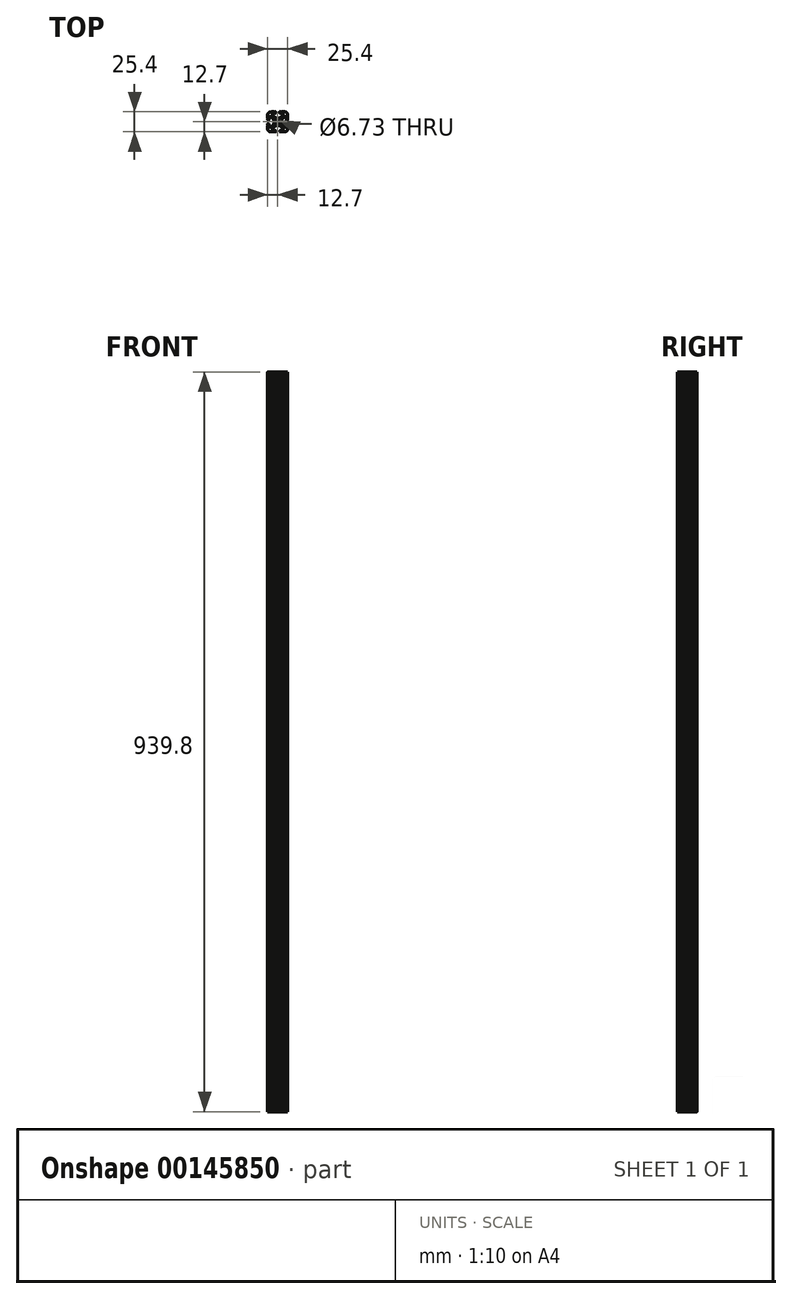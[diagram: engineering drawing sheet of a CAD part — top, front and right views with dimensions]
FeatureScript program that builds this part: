
annotation { "Feature Type Name" : "Feature", "Feature Type Description" : "" }
export const myFeature = defineFeature(function(context is Context, id is Id, definition is map)
    precondition{}
    {
        {
            var Q0;
            Q0=qCreatedBy(makeId("Top.planeOp"),FACE);
            var sketch = newSketch(context, id + "F0", { "sketchPlane" : qUnion([Q0])});
            skCircle(sketch, "E0", {"center": v(-12.7, 12.7) * mm, "radius": 3.36 * mm});
            skLineSegment(sketch, "E1.bottom", {"start": v(-11.24, 17.64) * mm, "end": v(-14.16, 17.64) * mm});
            skLineSegment(sketch, "E1.top", {"start": v(-11.24, 7.76) * mm, "end": v(-14.16, 7.76) * mm});
            skLineSegment(sketch, "E1.left", {"start": v(-7.76, 14.16) * mm, "end": v(-7.76, 11.24) * mm});
            skLineSegment(sketch, "E1.right", {"start": v(-17.64, 14.16) * mm, "end": v(-17.64, 11.24) * mm});
            skPoint(sketch, "E2.visualSharp", {"position": v(-25.4, 25.4) * mm});
            skPoint(sketch, "E3.visualSharp", {"position": v(0, 25.4) * mm});
            skPoint(sketch, "E4.visualSharp", {"position": v(0, 0) * mm});
            skPoint(sketch, "E5.visualSharp", {"position": v(-25.4, 0) * mm});
            skLineSegment(sketch, "E6.0", {"start": v(-18.7, 20.6) * mm, "end": v(-16.85, 18.76) * mm});
            skLineSegment(sketch, "E7.0", {"start": v(-20.6, 18.7) * mm, "end": v(-18.76, 16.85) * mm});
            skPoint(sketch, "E8.orphan", {"position": v(-23.85, 1.55) * mm});
            skPoint(sketch, "E9.orphan", {"position": v(-23.85, 23.85) * mm});
            skPoint(sketch, "E10.orphan", {"position": v(-1.55, 23.85) * mm});
            skPoint(sketch, "E11.orphan", {"position": v(-1.55, 1.55) * mm});
            skLineSegment(sketch, "E12", {"start": v(-8.55, 6.64) * mm, "end": v(-6.7, 4.8) * mm});
            skLineSegment(sketch, "E13.0", {"start": v(-18.7, 4.8) * mm, "end": v(-16.85, 6.64) * mm});
            skLineSegment(sketch, "E14.0", {"start": v(-20.6, 6.7) * mm, "end": v(-18.76, 8.55) * mm});
            skLineSegment(sketch, "E15.0", {"start": v(-8.55, 18.76) * mm, "end": v(-6.7, 20.6) * mm});
            skPoint(sketch, "E16.visualSharp", {"position": v(-23.85, 21.95) * mm});
            skArc(sketch, "E16.filletArc", {"start": v(-20.6, 18.7) * mm, "mid": v(-22.68, 19.1) * mm, "end": v(-23.85, 17.35) * mm});
            skPoint(sketch, "E17.visualSharp", {"position": v(-21.95, 23.85) * mm});
            skArc(sketch, "E17.filletArc", {"start": v(-17.35, 23.85) * mm, "mid": v(-19.1, 22.68) * mm, "end": v(-18.7, 20.6) * mm});
            skPoint(sketch, "E18.visualSharp", {"position": v(-5.34, 23.85) * mm});
            skLineSegment(sketch, "E19", {"start": v(-17.35, 23.85) * mm, "end": v(-15.58, 23.85) * mm});
            skLineSegment(sketch, "E20", {"start": v(-23.85, 17.35) * mm, "end": v(-23.85, 15.62) * mm});
            skLineSegment(sketch, "E21", {"start": v(-8.05, 1.55) * mm, "end": v(-9.78, 1.55) * mm});
            skArc(sketch, "E22.filletArc", {"start": v(-6.7, 20.6) * mm, "mid": v(-6.3, 22.68) * mm, "end": v(-8.05, 23.85) * mm});
            skPoint(sketch, "E23.visualSharp", {"position": v(-1.55, 3.45) * mm});
            skPoint(sketch, "E24.visualSharp", {"position": v(-3.45, 1.55) * mm});
            skArc(sketch, "E24.filletArc", {"start": v(-8.05, 1.55) * mm, "mid": v(-6.3, 2.73) * mm, "end": v(-6.7, 4.8) * mm});
            skArc(sketch, "E25.filletArc", {"start": v(-18.7, 4.8) * mm, "mid": v(-19.1, 2.73) * mm, "end": v(-17.35, 1.55) * mm});
            skArc(sketch, "E26.filletArc", {"start": v(-23.85, 8.05) * mm, "mid": v(-22.68, 6.3) * mm, "end": v(-20.6, 6.7) * mm});
            skLineSegment(sketch, "E27.bottom", {"start": v(-4.9, 0) * mm, "end": v(-8.05, 0) * mm});
            skLineSegment(sketch, "E27.top", {"start": v(-4.92, 25.4) * mm, "end": v(-8.05, 25.4) * mm});
            skLineSegment(sketch, "E27.left", {"start": v(0, 4.9) * mm, "end": v(0, 8.05) * mm});
            skLineSegment(sketch, "E27.right", {"start": v(-25.4, 4.9) * mm, "end": v(-25.4, 8.05) * mm});
            skArc(sketch, "E28.filletArc", {"start": v(-25.4, 3.81) * mm, "mid": v(-24.28, 1.12) * mm, "end": v(-21.59, 0) * mm});
            skArc(sketch, "E29.filletArc", {"start": v(-3.81, 0) * mm, "mid": v(-1.12, 1.12) * mm, "end": v(0, 3.8) * mm});
            skArc(sketch, "E30.filletArc", {"start": v(0, 21.59) * mm, "mid": v(-1.12, 24.28) * mm, "end": v(-3.8, 25.4) * mm});
            skArc(sketch, "E31.filletArc", {"start": v(-21.59, 25.4) * mm, "mid": v(-24.28, 24.28) * mm, "end": v(-25.4, 21.59) * mm});
            skPoint(sketch, "E32.newPointA", {"position": v(-17.64, 7.76) * mm});
            skArc(sketch, "E32.filletArc", {"start": v(-14.16, 7.76) * mm, "mid": v(-15.62, 7.47) * mm, "end": v(-16.85, 6.64) * mm});
            skPoint(sketch, "E33.newPointA", {"position": v(-7.76, 7.76) * mm});
            skArc(sketch, "E33.filletArc", {"start": v(-8.55, 6.64) * mm, "mid": v(-9.78, 7.47) * mm, "end": v(-11.24, 7.76) * mm});
            skArc(sketch, "E34.filletArc", {"start": v(-7.76, 11.24) * mm, "mid": v(-7.47, 9.78) * mm, "end": v(-6.64, 8.55) * mm});
            skArc(sketch, "E35.filletArc", {"start": v(-6.64, 16.85) * mm, "mid": v(-7.47, 15.62) * mm, "end": v(-7.76, 14.16) * mm});
            skPoint(sketch, "E36.newPointB", {"position": v(-7.76, 17.64) * mm});
            skArc(sketch, "E36.filletArc", {"start": v(-11.24, 17.64) * mm, "mid": v(-9.78, 17.93) * mm, "end": v(-8.55, 18.76) * mm});
            skPoint(sketch, "E37.newPointB", {"position": v(-17.64, 17.64) * mm});
            skArc(sketch, "E37.filletArc", {"start": v(-16.85, 18.76) * mm, "mid": v(-15.62, 17.93) * mm, "end": v(-14.16, 17.64) * mm});
            skArc(sketch, "E38.filletArc", {"start": v(-17.64, 14.16) * mm, "mid": v(-17.93, 15.62) * mm, "end": v(-18.76, 16.85) * mm});
            skArc(sketch, "E39.filletArc", {"start": v(-18.76, 8.55) * mm, "mid": v(-17.93, 9.78) * mm, "end": v(-17.64, 11.24) * mm});
            skLineSegment(sketch, "E40", {"start": v(-6.64, 8.55) * mm, "end": v(-4.8, 6.7) * mm});
            skPoint(sketch, "E41.visualSharp", {"position": v(-1.55, 21.95) * mm});
            skArc(sketch, "E42.filletArc", {"start": v(-4.8, 6.7) * mm, "mid": v(-2.73, 6.3) * mm, "end": v(-1.55, 8.05) * mm});
            skLineSegment(sketch, "E43", {"start": v(-1.55, 8.05) * mm, "end": v(-1.55, 9.78) * mm});
            skLineSegment(sketch, "E44", {"start": v(-6.64, 16.85) * mm, "end": v(-4.8, 18.7) * mm});
            skArc(sketch, "E45.filletArc", {"start": v(-1.55, 17.35) * mm, "mid": v(-2.73, 19.1) * mm, "end": v(-4.8, 18.7) * mm});
            skArc(sketch, "E46", {"start": v(-23.85, 9.78) * mm, "mid": v(-24.63, 10.56) * mm, "end": v(-25.4, 9.78) * mm});
            skArc(sketch, "E47", {"start": v(-25.4, 15.62) * mm, "mid": v(-24.63, 14.86) * mm, "end": v(-23.85, 15.62) * mm});
            skArc(sketch, "E48", {"start": v(-15.62, 23.85) * mm, "mid": v(-14.83, 24.63) * mm, "end": v(-15.62, 25.4) * mm});
            skArc(sketch, "E49", {"start": v(-9.78, 25.4) * mm, "mid": v(-10.6, 24.63) * mm, "end": v(-9.78, 23.85) * mm});
            skArc(sketch, "E50", {"start": v(-1.55, 15.62) * mm, "mid": v(-0.77, 14.88) * mm, "end": v(0, 15.62) * mm});
            skArc(sketch, "E51", {"start": v(0, 9.78) * mm, "mid": v(-0.77, 10.5) * mm, "end": v(-1.55, 9.78) * mm});
            skArc(sketch, "E52", {"start": v(-9.78, 1.55) * mm, "mid": v(-10.4, 0.77) * mm, "end": v(-9.78, 0) * mm});
            skArc(sketch, "E53", {"start": v(-15.62, 0) * mm, "mid": v(-14.85, 0.77) * mm, "end": v(-15.62, 1.55) * mm});
            skLineSegment(sketch, "E54.trimOffspring", {"start": v(-15.62, 1.55) * mm, "end": v(-17.35, 1.55) * mm});
            skLineSegment(sketch, "E55.trimOffspring", {"start": v(-16.7, 0) * mm, "end": v(-20.5, 0) * mm});
            skLineSegment(sketch, "E56.trimOffspring", {"start": v(-1.55, 15.62) * mm, "end": v(-1.55, 17.35) * mm});
            skLineSegment(sketch, "E57.trimOffspring", {"start": v(0, 15.62) * mm, "end": v(0, 16.26) * mm});
            skLineSegment(sketch, "E58.trimOffspring", {"start": v(-23.85, 9.78) * mm, "end": v(-23.85, 8.05) * mm});
            skLineSegment(sketch, "E59.trimOffspring", {"start": v(-25.4, 15.62) * mm, "end": v(-25.4, 16.26) * mm});
            skLineSegment(sketch, "E60.trimOffspring", {"start": v(-9.86, 23.85) * mm, "end": v(-8.05, 23.85) * mm});
            skLineSegment(sketch, "E61.trimOffspring", {"start": v(-15.58, 25.4) * mm, "end": v(-16.25, 25.4) * mm});
            skPoint(sketch, "E62.start.orphan", {"position": v(-15.62, 17.93) * mm});
            skPoint(sketch, "E63.start.orphan", {"position": v(-9.78, 17.93) * mm});
            skPoint(sketch, "E64.start.orphan", {"position": v(-7.47, 15.62) * mm});
            skPoint(sketch, "E65.start.orphan", {"position": v(-7.47, 9.78) * mm});
            skPoint(sketch, "E66.start.orphan", {"position": v(-17.93, 15.62) * mm});
            skPoint(sketch, "E67.start.orphan", {"position": v(-17.93, 9.78) * mm});
            skPoint(sketch, "E68.start.orphan", {"position": v(-9.78, 7.47) * mm});
            skPoint(sketch, "E69.start.orphan", {"position": v(-15.62, 7.47) * mm});
            skPoint(sketch, "E70.endSnap0", {"position": v(0, 18.6) * mm});
            skPoint(sketch, "E71.startSnap0", {"position": v(-1.55, 8.92) * mm});
            skArc(sketch, "E72", {"start": v(-4.92, 25.4) * mm, "mid": v(-4.37, 24.9) * mm, "end": v(-3.81, 25.4) * mm});
            skArc(sketch, "E73", {"start": v(-9.14, 25.4) * mm, "mid": v(-8.6, 24.86) * mm, "end": v(-8.05, 25.4) * mm});
            skArc(sketch, "E74", {"start": v(-17.35, 25.4) * mm, "mid": v(-16.8, 24.86) * mm, "end": v(-16.25, 25.4) * mm});
            skArc(sketch, "E75", {"start": v(-21.59, 25.4) * mm, "mid": v(-21.04, 24.85) * mm, "end": v(-20.49, 25.4) * mm});
            skLineSegment(sketch, "E76", {"start": v(-25.4, 21.59) * mm, "end": v(-25.4, 20.5) * mm});
            skArc(sketch, "E77", {"start": v(-25.4, 16.26) * mm, "mid": v(-24.84, 16.8) * mm, "end": v(-25.4, 17.35) * mm});
            skArc(sketch, "E78", {"start": v(-25.4, 8.05) * mm, "mid": v(-24.9, 8.6) * mm, "end": v(-25.4, 9.15) * mm});
            skArc(sketch, "E79", {"start": v(-25.4, 3.81) * mm, "mid": v(-24.85, 4.36) * mm, "end": v(-25.4, 4.9) * mm});
            skArc(sketch, "E80", {"start": v(-20.5, 0) * mm, "mid": v(-21.04, 0.55) * mm, "end": v(-21.59, 0) * mm});
            skArc(sketch, "E81", {"start": v(-15.62, 0) * mm, "mid": v(-16.16, 0.54) * mm, "end": v(-16.7, 0) * mm});
            skArc(sketch, "E82", {"start": v(-8.05, 0) * mm, "mid": v(-8.6, 0.55) * mm, "end": v(-9.15, 0) * mm});
            skArc(sketch, "E83", {"start": v(-3.81, 0) * mm, "mid": v(-4.35, 0.54) * mm, "end": v(-4.9, 0) * mm});
            skLineSegment(sketch, "E84.trimOffspring", {"start": v(-17.35, 25.4) * mm, "end": v(-20.49, 25.4) * mm});
            skLineSegment(sketch, "E85.trimOffspring", {"start": v(-25.4, 17.35) * mm, "end": v(-25.4, 21.59) * mm});
            skLineSegment(sketch, "E86.trimOffspring", {"start": v(-25.4, 9.15) * mm, "end": v(-25.4, 9.78) * mm});
            skLineSegment(sketch, "E87.trimOffspring", {"start": v(-9.15, 0) * mm, "end": v(-9.78, 0) * mm});
            skArc(sketch, "E88", {"start": v(0, 4.9) * mm, "mid": v(-0.54, 4.36) * mm, "end": v(0, 3.8) * mm});
            skArc(sketch, "E89", {"start": v(0, 9.15) * mm, "mid": v(-0.54, 8.6) * mm, "end": v(0, 8.05) * mm});
            skLineSegment(sketch, "E90.trimOffspring", {"start": v(0, 9.15) * mm, "end": v(0, 9.78) * mm});
            skArc(sketch, "E91", {"start": v(0, 21.59) * mm, "mid": v(-0.55, 21.04) * mm, "end": v(0, 20.5) * mm});
            skArc(sketch, "E92", {"start": v(0, 17.35) * mm, "mid": v(-0.55, 16.8) * mm, "end": v(0, 16.26) * mm});
            skLineSegment(sketch, "E93.trimOffspring", {"start": v(0, 17.35) * mm, "end": v(0, 20.5) * mm});
            skLineSegment(sketch, "E94.trimOffspring", {"start": v(-9.14, 25.4) * mm, "end": v(-9.86, 25.4) * mm});
            skSolve(sketch);
        }
        {
            var Q0;
            Q0=qSketchRegion(id+"F0",true);
            extrude(context, id + "F1", {"entities" : qUnion([Q0]), "depth" : 939.8 * mm});
        }
    });
